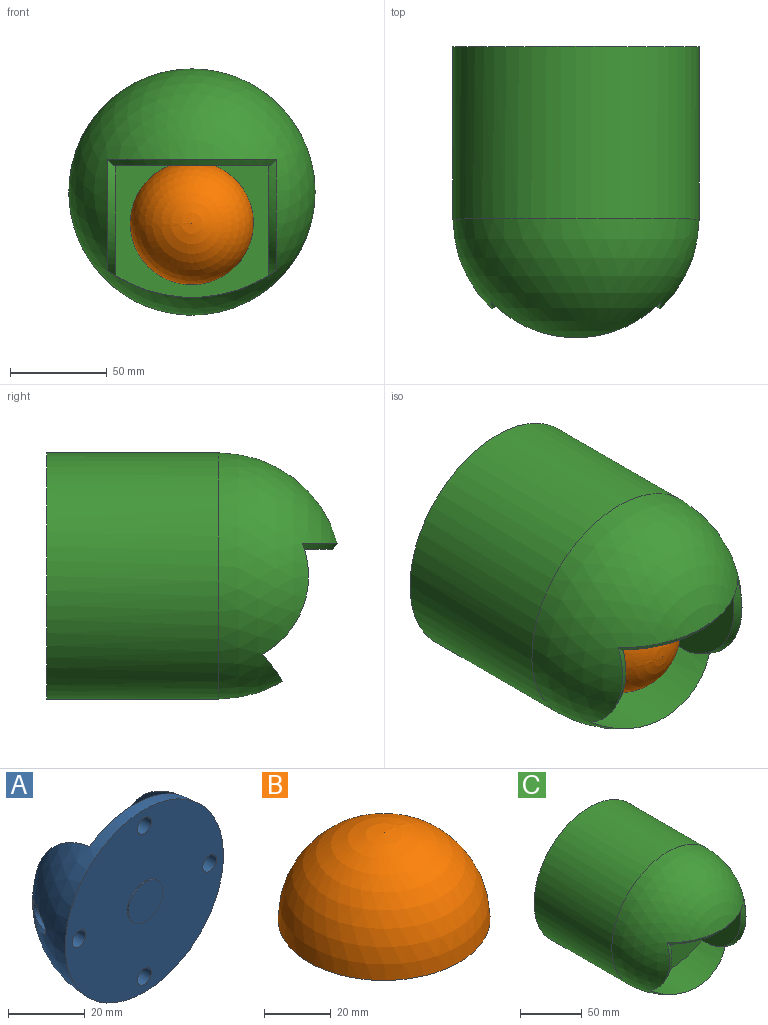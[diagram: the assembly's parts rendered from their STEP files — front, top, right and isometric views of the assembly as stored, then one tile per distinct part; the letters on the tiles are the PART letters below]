
ASSEMBLY  parts=3 mates=2
PART A: 30 faces, bbox 58.4x24.7x58.4 mm
  f0: cylinder r=2.54mm len=5.08mm, axis (0,1,0), area 60.8mm2, adj f7,f29
  f1: cylinder r=2.54mm len=5.08mm, axis (0,1,0), area 60.8mm2, adj f7,f28
  f2: plane 15.17x8.76mm, normal (0,0.87,-0.5), area 70.5mm2, adj f11,f12,f17,f26
  f3: sphere r=29.21mm, area 2456.1mm2, adj f5,f6,f7,f18,f19,f28,f29
  f4: plane 15.17x8.76mm, normal (0,0.87,-0.5), area 70.5mm2, adj f11,f13,f16,f25
  f5: plane 47.59x21.56mm, normal (-1,0,0), area 505.1mm2, adj f3,f8,f9,f10,f11,f28,f29
  f6: plane 47.59x21.56mm, normal (1,0,0), area 505.1mm2, adj f3,f8,f9,f10,f11,f28,f29
  f7: plane 58.42x58.42mm, normal (0,-1,0), area 2472.7mm2, adj f0,f1,f3,f14,f15,f21
  f8: cylinder r=19.05mm len=33.02mm, axis (0,1,0), area 50.7mm2, adj f5,f6,f10,f28
  f9: cylinder r=19.05mm len=33.02mm, axis (0,1,0), area 50.7mm2, adj f5,f6,f10,f29
  f10: plane 38.1x33.02mm, normal (0,1,0), area 1074.8mm2, adj f5,f6,f8,f9
  f11: cylinder r=8.89mm len=33.02mm, axis (1,0,0), area 1180.1mm2, adj f2,f4,f5,f6,f16,f17,f24,f27
  f12: plane 14.42x10.91mm, normal (-1,0,0), area 80.7mm2, adj f2,f17
  f13: plane 14.42x10.91mm, normal (1,0,0), area 80.7mm2, adj f4,f16
  f14: cylinder r=2.54mm len=19.41mm, axis (0,1,0), area 230.3mm2, adj f7,f18
  f15: cylinder r=2.54mm len=19.41mm, axis (0,1,0), area 226.8mm2, adj f7,f19
  f16: cone r=8.89mm half-angle=45deg, axis (-1,0,0), area 22.8mm2, adj f4,f11,f13
  f17: cone r=8.21mm half-angle=45deg, axis (1,0,0), area 22.8mm2, adj f2,f11,f12
  f18: bspline ~11.73x6.59mm, area 30.5mm2, adj f3,f14
  f19: bspline ~11.73x6.59mm, area 30.5mm2, adj f3,f15
  f20: plane 18.8x13.84mm, normal (0,0.87,-0.5), area 81mm2, adj f23,f24,f25,f26,f27
  f21: cylinder r=6.35mm len=12.7mm, axis (0,1,0), area 20.3mm2, adj f7,f22
  f22: plane 12.7x12.7mm, normal (0,-1,0), area 126.7mm2, adj f21
  f23: sphere r=16.79mm, area 187.6mm2, adj f20
  f24: cylinder r=0.76mm len=10.31mm, axis (1,0,0), area 12.1mm2, adj f11,f20,f25,f26
  f25: torus R=9.4mm, axis (0,0.87,-0.5), area 24.3mm2, adj f4,f20,f24,f27
  f26: torus R=9.4mm, axis (0,0.87,-0.5), area 24.3mm2, adj f2,f20,f24,f27
  f27: cylinder r=0.76mm len=10.31mm, axis (-1,0,0), area 12.1mm2, adj f11,f20,f25,f26
  f28: plane 33.02x19.46mm, normal (0,1,0), area 343.9mm2, adj f1,f3,f5,f6,f8
  f29: plane 33.02x19.46mm, normal (0,1,0), area 343.9mm2, adj f0,f3,f5,f6,f9
PART B: 3 faces, bbox 63.5x63.5x31.8 mm
  f0: plane 63.5x63.5mm, normal (0,0,-1), area 248.3mm2, adj f1,f2
  f1: sphere r=31.75mm, area 6333.8mm2, adj f0
  f2: sphere r=30.48mm, area 5837.3mm2, adj f0
PART C: 11 faces, bbox 127x150.2x127 mm
  f0: cylinder r=63.5mm len=127mm, axis (0,1,0), area 35469.5mm2, adj f1,f2
  f1: plane 127x127mm, normal (0,1,0), area 12667.7mm2, adj f0
  f2: sphere r=63.5mm, area 17979.7mm2, adj f0,f3,f8,f9,f10
  f3: cylinder r=74.84mm len=87.03mm, axis (0,-1,0), area 2574.4mm2, adj f2,f4,f6,f7,f8,f10
  f4: plane 56.92x44.45mm, normal (-1,0,0), area 2143.9mm2, adj f3,f5,f7,f10
  f5: plane 80.87x58.85mm, normal (0,0,-1), area 4261.8mm2, adj f4,f6,f7,f8,f9,f10
  f6: plane 56.92x44.45mm, normal (1,0,0), area 2143.9mm2, adj f3,f5,f7,f8
  f7: plane 78.74x68.11mm, normal (0,-1,0), area 5078.8mm2, adj f3,f4,f5,f6
  f8: cone r=46.24mm half-angle=23.4deg, axis (-1,0,0), area 310.5mm2, adj f2,f3,f5,f6,f9
  f9: cone r=58.85mm half-angle=37.3deg, axis (0,0,1), area 363.8mm2, adj f2,f5,f8,f10
  f10: cone r=44.45mm half-angle=23.4deg, axis (1,0,0), area 310.5mm2, adj f2,f3,f4,f5,f9
PLACE A rot(axis=(-0.02,0,1),180deg) t=(-84.09,-107.14,133.56)mm
PLACE B rot(axis=(0.01,0.71,-0.71),178.6deg) t=(-84.09,-77.93,133.56)mm
PLACE C t=(-84,10.97,149.62)mm fixed
MATE fastened B.f0 <-> A.f21  axis (0,1,0) through (-84.09,-77.93,133.56)mm
MATE revolute A.f7 <-> C.f7  axis (0,1,0) through (-84,-77.93,131.03)mm
